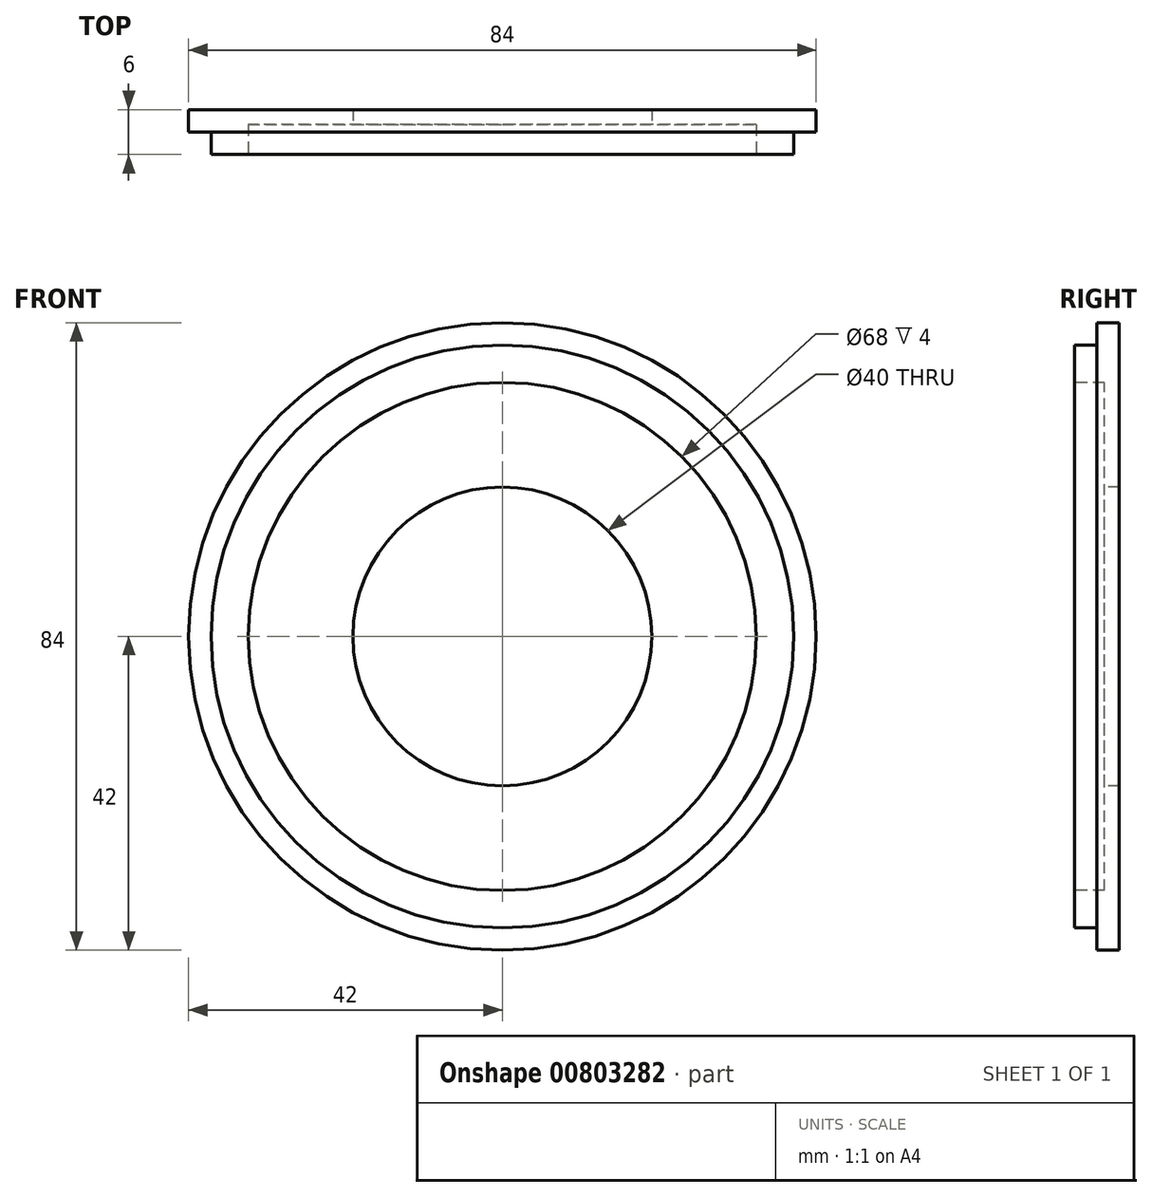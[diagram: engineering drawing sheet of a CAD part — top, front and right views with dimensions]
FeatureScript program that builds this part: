
annotation { "Feature Type Name" : "Feature", "Feature Type Description" : "" }
export const myFeature = defineFeature(function(context is Context, id is Id, definition is map)
    precondition{}
    {
        {
            var Q0;
            Q0=qCreatedBy(makeId("Front.planeOp"),FACE);
            var sketch = newSketch(context, id + "F0", { "sketchPlane" : qUnion([Q0])});
            skCircle(sketch, "E0", {"center": v(0, 0) * mm, "radius": 42 * mm});
            skSolve(sketch);
        }
        {
            var Q0;
            Q0 = qSketchRegion(id + "F0", true);
            extrude(context, id + "F1", {"entities" : qUnion([Q0]), "oppositeDirection" : true, "depth" : 6 * mm, "offsetDistance" : 25 * mm});
        }
        {
            var Q0;
            Q0=makeQuery(id+"F1.opExtrude","CAP_FACE",FACE,{"disambiguationData":[OSD([sQuery(id+"F0.wireOp",EDGE,"E0")])],"isStart":true});
            var sketch = newSketch(context, id + "F2", { "sketchPlane" : qUnion([Q0])});
            skCircle(sketch, "E1", {"center": v(0, 0) * mm, "radius": 34 * mm});
            skSolve(sketch);
        }
        {
            var Q0;
            Q0=makeQuery(id+"F2.imprint","IMPRINT",FACE,{"disambiguationData":[TD([[makeQuery(id+"F2.imprint","IMPRINT",EDGE,{"derivedFrom":sQuery(id+"F2.wireOp",EDGE,"E1")}),1.0]])]});
            extrude(context, id + "F3", {"entities" : qUnion([Q0]), "operationType" : NewBodyOperationType.REMOVE, "oppositeDirection" : true, "depth" : 4 * mm, "offsetDistance" : 25 * mm});
        }
        {
            var Q0;
            Q0=makeQuery(id+"F3.boolean.opBoolean","COPY",FACE,{"derivedFrom":makeQuery(id+"F3.opExtrude","CAP_FACE",FACE,{"disambiguationData":[OSD([sQuery(id+"F2.wireOp",EDGE,"E1")])],"isStart":false})});
            var sketch = newSketch(context, id + "F4", { "sketchPlane" : qUnion([Q0])});
            skCircle(sketch, "E2", {"center": v(0, 0) * mm, "radius": 20 * mm});
            skSolve(sketch);
        }
        {
            var Q0;
            Q0=makeQuery(id+"F4.imprint","IMPRINT",FACE,{"disambiguationData":[TD([[makeQuery(id+"F4.imprint","IMPRINT",EDGE,{"derivedFrom":sQuery(id+"F4.wireOp",EDGE,"E2")}),1.0]])]});
            extrude(context, id + "F5", {"entities" : qUnion([Q0]), "operationType" : NewBodyOperationType.REMOVE, "oppositeDirection" : true, "depth" : 2 * mm, "offsetDistance" : 25 * mm});
        }
        {
            var Q0;
            Q0=makeQuery(id+"F1.opExtrude","CAP_FACE",FACE,{"disambiguationData":[OSD([sQuery(id+"F0.wireOp",EDGE,"E0")])],"isStart":true});
            var sketch = newSketch(context, id + "F6", { "sketchPlane" : qUnion([Q0])});
            skCircle(sketch, "E3", {"center": v(0, 0) * mm, "radius": 39 * mm});
            skSolve(sketch);
        }
        {
            var Q0;
            Q0=makeQuery(id+"F6.imprint","IMPRINT",FACE,{"disambiguationData":[TD([[makeQuery(id+"F6.imprint","IMPRINT",EDGE,{"derivedFrom":sQuery(id+"F6.wireOp",EDGE,"E3")}),-1.0]])]});
            extrude(context, id + "F7", {"entities" : qUnion([Q0]), "operationType" : NewBodyOperationType.REMOVE, "oppositeDirection" : true, "depth" : 3 * mm, "offsetDistance" : 25 * mm});
        }
    });
